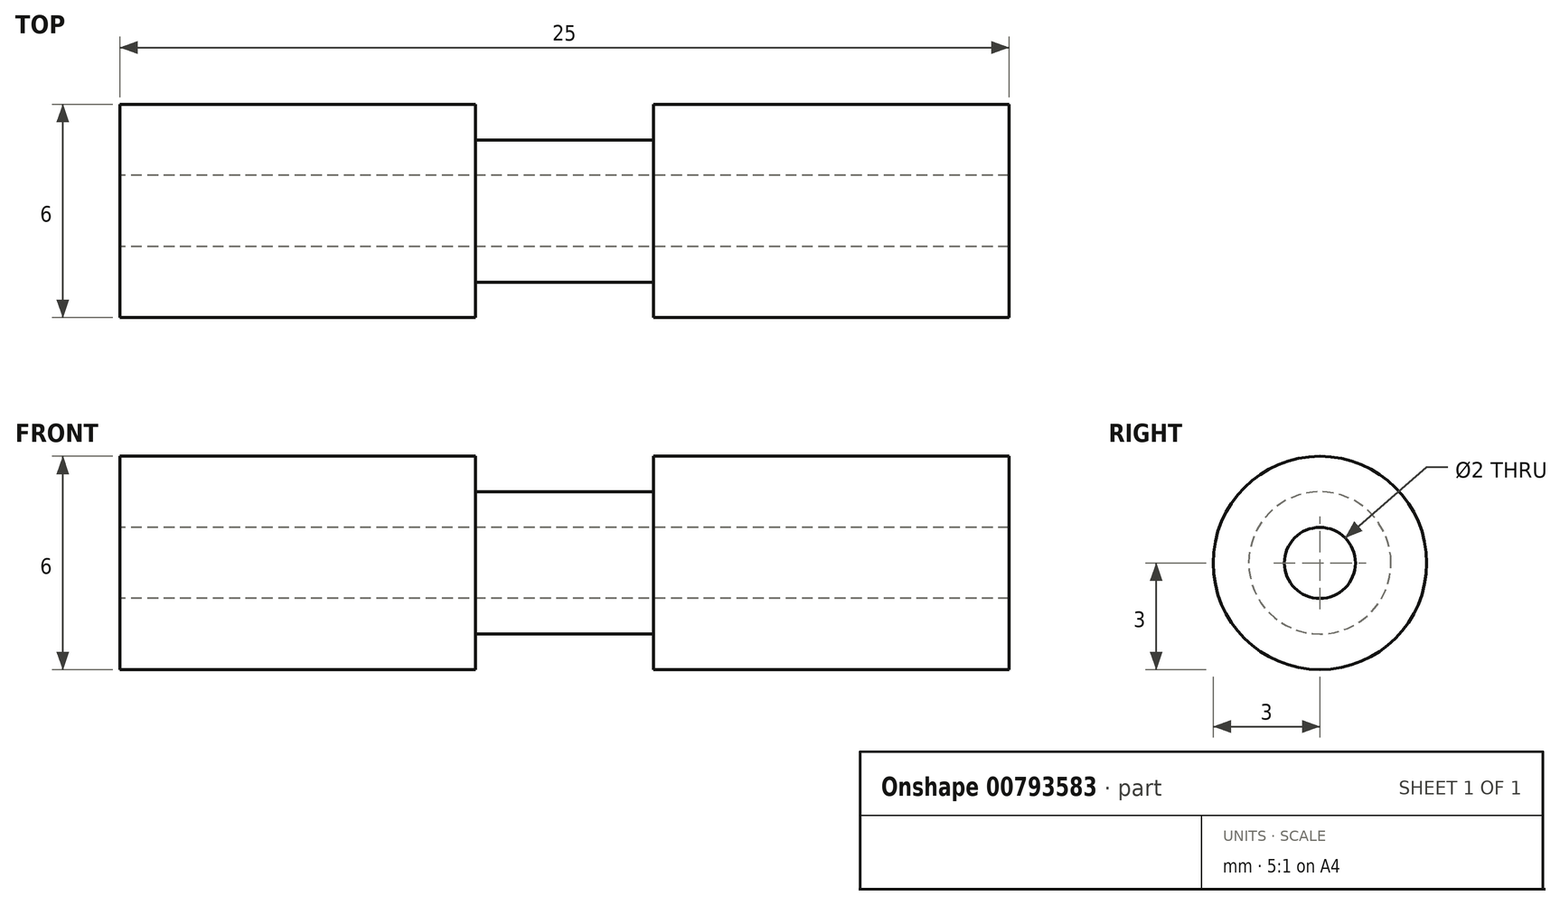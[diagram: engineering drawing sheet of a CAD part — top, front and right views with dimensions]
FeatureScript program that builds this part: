
annotation { "Feature Type Name" : "Feature", "Feature Type Description" : "" }
export const myFeature = defineFeature(function(context is Context, id is Id, definition is map)
    precondition{}
    {
        {
            var Q0;
            Q0=qCreatedBy(makeId("Top.planeOp"),FACE);
            var sketch = newSketch(context, id + "F0", { "sketchPlane" : qUnion([Q0])});
            skLineSegment(sketch, "E0", {"start": v(0, 0) * mm, "end": v(0, 3) * mm});
            skLineSegment(sketch, "E1", {"start": v(0, 3) * mm, "end": v(10, 3) * mm});
            skLineSegment(sketch, "E2", {"start": v(10, 3) * mm, "end": v(10, 2) * mm});
            skLineSegment(sketch, "E3", {"start": v(10, 2) * mm, "end": v(15, 2) * mm});
            skLineSegment(sketch, "E4", {"start": v(15, 2) * mm, "end": v(15, 3) * mm});
            skLineSegment(sketch, "E5", {"start": v(15, 3) * mm, "end": v(25, 3) * mm});
            skLineSegment(sketch, "E6", {"start": v(25, 3) * mm, "end": v(25, 0) * mm});
            skLineSegment(sketch, "E7", {"start": v(0, 0) * mm, "end": v(25, 0) * mm});
            skSolve(sketch);
        }
        {
            var Q0;
            Q0 = qSketchRegion(id + "F0", true);
            var Q1;
            Q1=sQuery(id+"F0.wireOp",EDGE,"E7");
            revolve(context, id + "F1", {"surfaceOperationType" : NewSurfaceOperationType.NEW, "entities" : qUnion([Q0]), "axis" : qUnion([Q1]), "revolveType" : RevolveType.FULL});
        }
        {
            var Q0;
            Q0=makeQuery(id+"F1.opRevolve","SWEPT_FACE",FACE,{"disambiguationData":[OSD([sQuery(id+"F0.wireOp",EDGE,"E0")])]});
            var sketch = newSketch(context, id + "F2", { "sketchPlane" : qUnion([Q0])});
            skCircle(sketch, "E8", {"center": v(0, 0) * mm, "radius": 1 * mm});
            skSolve(sketch);
        }
        {
            var Q0;
            Q0=makeQuery(id+"F2.imprint","IMPRINT",FACE,{"disambiguationData":[TD([[makeQuery(id+"F2.imprint","IMPRINT",EDGE,{"derivedFrom":sQuery(id+"F2.wireOp",EDGE,"E8")}),1.0]])]});
            extrude(context, id + "F3", {"entities" : qUnion([Q0]), "operationType" : NewBodyOperationType.REMOVE, "endBound" : BoundingType.THROUGH_ALL, "oppositeDirection" : true, "depth" : 25 * mm, "offsetDistance" : 25 * mm});
        }
    });
